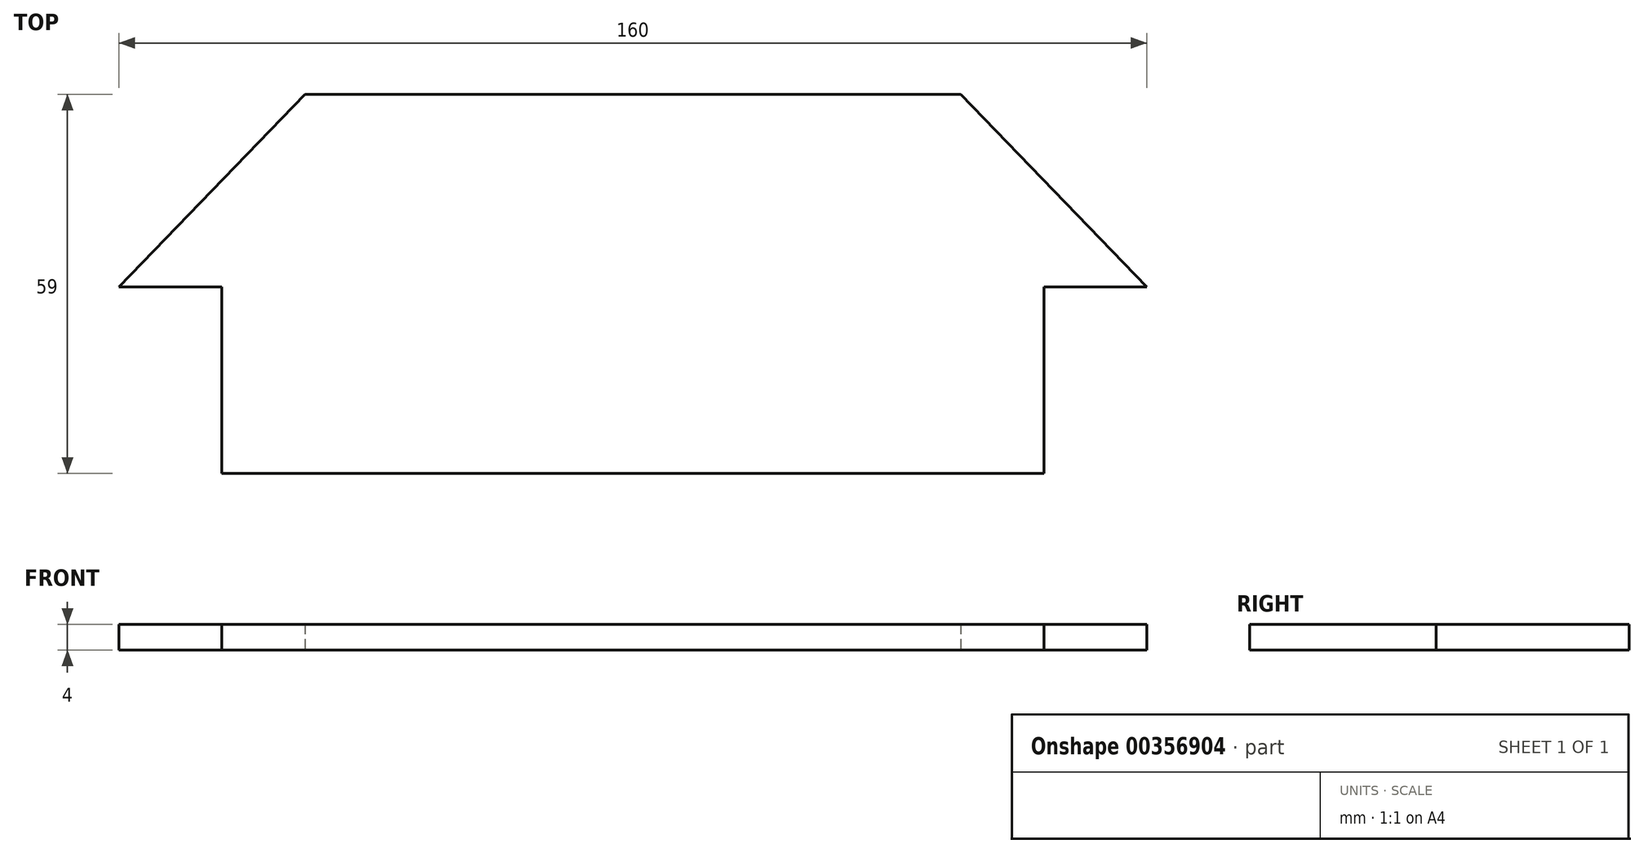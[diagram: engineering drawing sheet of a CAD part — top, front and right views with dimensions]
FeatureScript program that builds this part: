
annotation { "Feature Type Name" : "Feature", "Feature Type Description" : "" }
export const myFeature = defineFeature(function(context is Context, id is Id, definition is map)
    precondition{}
    {
        {
            var Q0;
            Q0=qCreatedBy(makeId("Top.planeOp"),FACE);
            var sketch = newSketch(context, id + "F0", { "sketchPlane" : qUnion([Q0])});
            skLineSegment(sketch, "E0.bottom", {"start": v(-45, 27.5) * mm, "end": v(57, 27.5) * mm});
            skLineSegment(sketch, "E0.top", {"start": v(-58, -31.5) * mm, "end": v(70, -31.5) * mm});
            skPoint(sketch, "E0.middle", {"position": v(0, 0) * mm});
            skLineSegment(sketch, "E1", {"start": v(-58, -31.5) * mm, "end": v(-58, -2.5) * mm});
            skLineSegment(sketch, "E2", {"start": v(-58, -2.5) * mm, "end": v(-74, -2.5) * mm});
            skLineSegment(sketch, "E3", {"start": v(-74, -2.5) * mm, "end": v(-45, 27.5) * mm});
            skLineSegment(sketch, "E4", {"start": v(70, -31.5) * mm, "end": v(70, -2.5) * mm});
            skLineSegment(sketch, "E5", {"start": v(70, -2.5) * mm, "end": v(86, -2.5) * mm});
            skLineSegment(sketch, "E6", {"start": v(57, 27.5) * mm, "end": v(86, -2.5) * mm});
            skSolve(sketch);
        }
        {
            var Q0;
            Q0=qSketchRegion(id+"F0",true);
            extrude(context, id + "F1", {"entities" : qUnion([Q0]), "depth" : 4 * mm});
        }
    });
